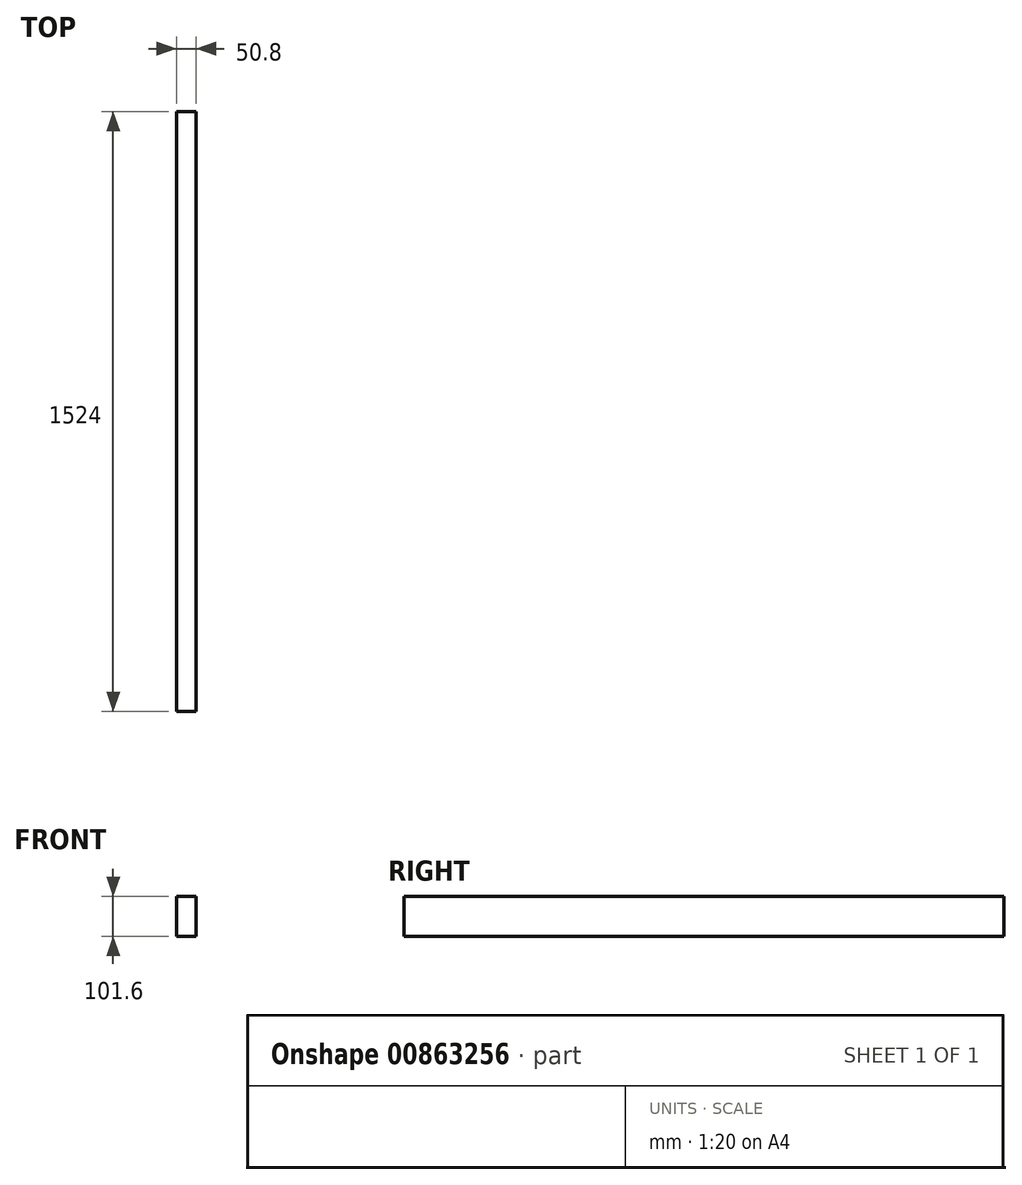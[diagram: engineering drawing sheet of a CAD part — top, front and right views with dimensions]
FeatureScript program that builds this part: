
annotation { "Feature Type Name" : "Feature", "Feature Type Description" : "" }
export const myFeature = defineFeature(function(context is Context, id is Id, definition is map)
    precondition{}
    {
        {
            var Q0;
            Q0=qCreatedBy(makeId("Front.planeOp"),FACE);
            var sketch = newSketch(context, id + "F0", { "sketchPlane" : qUnion([Q0])});
            skLineSegment(sketch, "E0.bottom", {"start": v(0, 0) * mm, "end": v(50.8, 0) * mm});
            skLineSegment(sketch, "E0.top", {"start": v(0, 101.6) * mm, "end": v(50.8, 101.6) * mm});
            skLineSegment(sketch, "E0.left", {"start": v(0, 0) * mm, "end": v(0, 101.6) * mm});
            skLineSegment(sketch, "E0.right", {"start": v(50.8, 0) * mm, "end": v(50.8, 101.6) * mm});
            skSolve(sketch);
        }
        {
            var Q0;
            Q0=makeQuery(id+"F0.imprint","IMPRINT",FACE,{"disambiguationData":[TD([[makeQuery(id+"F0.imprint","IMPRINT",EDGE,{"derivedFrom":sQuery(id+"F0.wireOp",EDGE,"E0.bottom")}),1.0]])]});
            extrude(context, id + "F1", {"entities" : qUnion([Q0]), "depth" : 1524 * mm, "offsetDistance" : 25.4 * mm});
        }
    });
